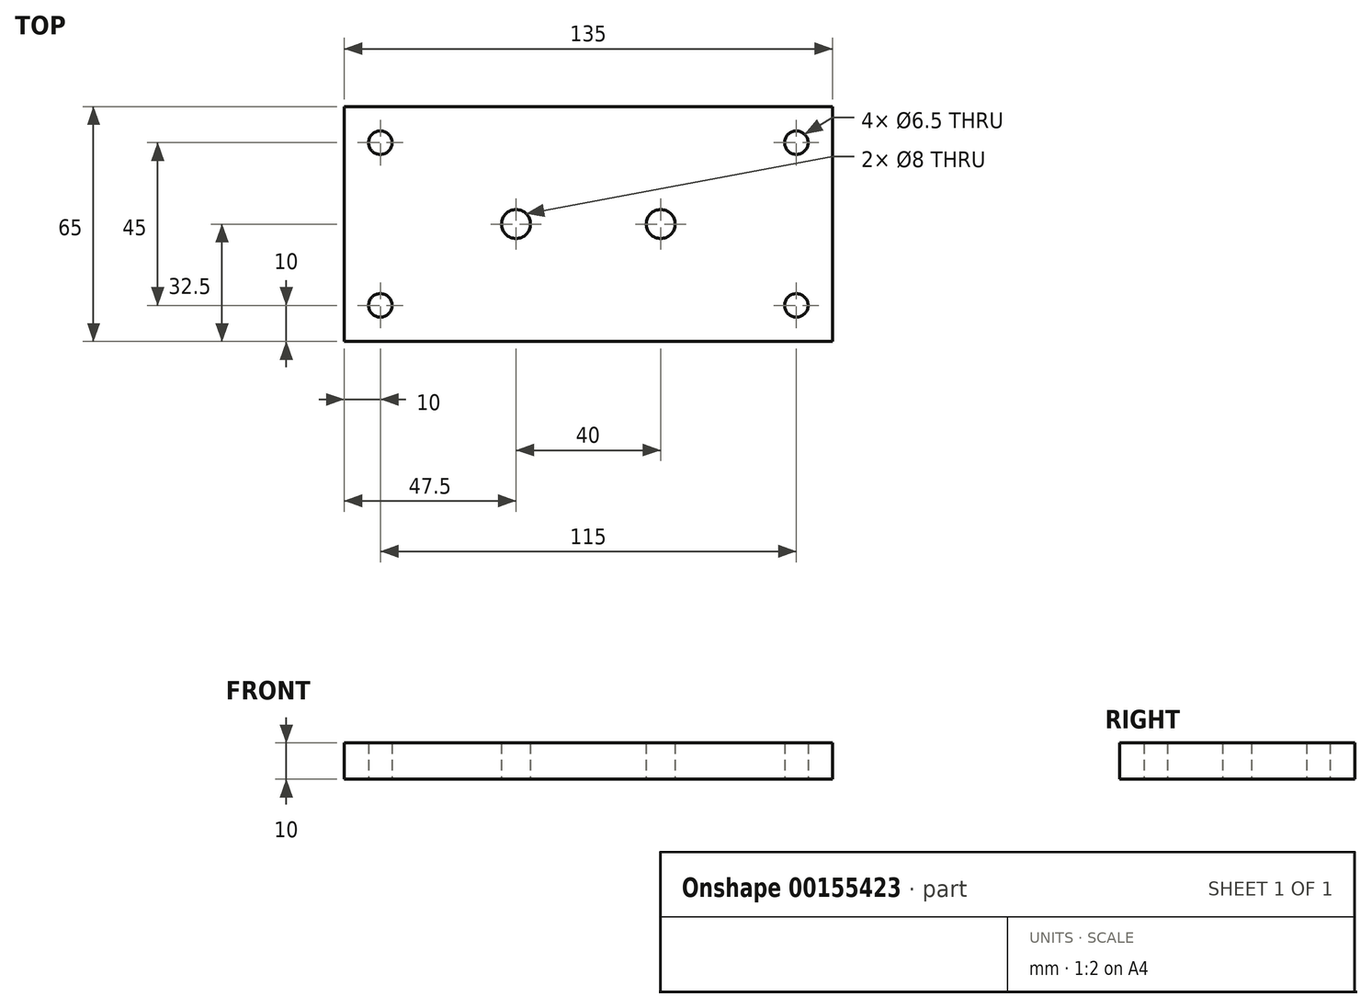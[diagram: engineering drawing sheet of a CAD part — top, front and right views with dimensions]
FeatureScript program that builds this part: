
annotation { "Feature Type Name" : "Feature", "Feature Type Description" : "" }
export const myFeature = defineFeature(function(context is Context, id is Id, definition is map)
    precondition{}
    {
        {
            var Q0;
            Q0=qCreatedBy(makeId("Top.planeOp"),FACE);
            var sketch = newSketch(context, id + "F0", { "sketchPlane" : qUnion([Q0])});
            skLineSegment(sketch, "E0.bottom", {"start": v(67.5, -32.5) * mm, "end": v(-67.5, -32.5) * mm});
            skLineSegment(sketch, "E0.top", {"start": v(67.5, 32.5) * mm, "end": v(-67.5, 32.5) * mm});
            skLineSegment(sketch, "E0.left", {"start": v(67.5, -32.5) * mm, "end": v(67.5, 32.5) * mm});
            skLineSegment(sketch, "E0.right", {"start": v(-67.5, -32.5) * mm, "end": v(-67.5, 32.5) * mm});
            skPoint(sketch, "E0.middle", {"position": v(0, 0) * mm});
            skCircle(sketch, "E1", {"center": v(-57.5, 22.5) * mm, "radius": 3.25 * mm});
            skCircle(sketch, "E2.MirrorC", {"center": v(57.5, 22.5) * mm, "radius": 3.25 * mm});
            skCircle(sketch, "E3.MirrorC", {"center": v(-57.5, -22.5) * mm, "radius": 3.25 * mm});
            skCircle(sketch, "E4.MirrorC", {"center": v(57.5, -22.5) * mm, "radius": 3.25 * mm});
            skCircle(sketch, "E5", {"center": v(-20, 0) * mm, "radius": 4 * mm});
            skCircle(sketch, "E6.MirrorC", {"center": v(20, 0) * mm, "radius": 4 * mm});
            skSolve(sketch);
        }
        {
            var Q0;
            Q0=makeQuery(id+"F0.imprint","IMPRINT",FACE,{"disambiguationData":[TD([[makeQuery(id+"F0.imprint","IMPRINT",EDGE,{"derivedFrom":sQuery(id+"F0.wireOp",EDGE,"E0.bottom")}),-1.0]])]});
            extrude(context, id + "F1", {"entities" : qUnion([Q0]), "depth" : 10 * mm});
        }
    });
